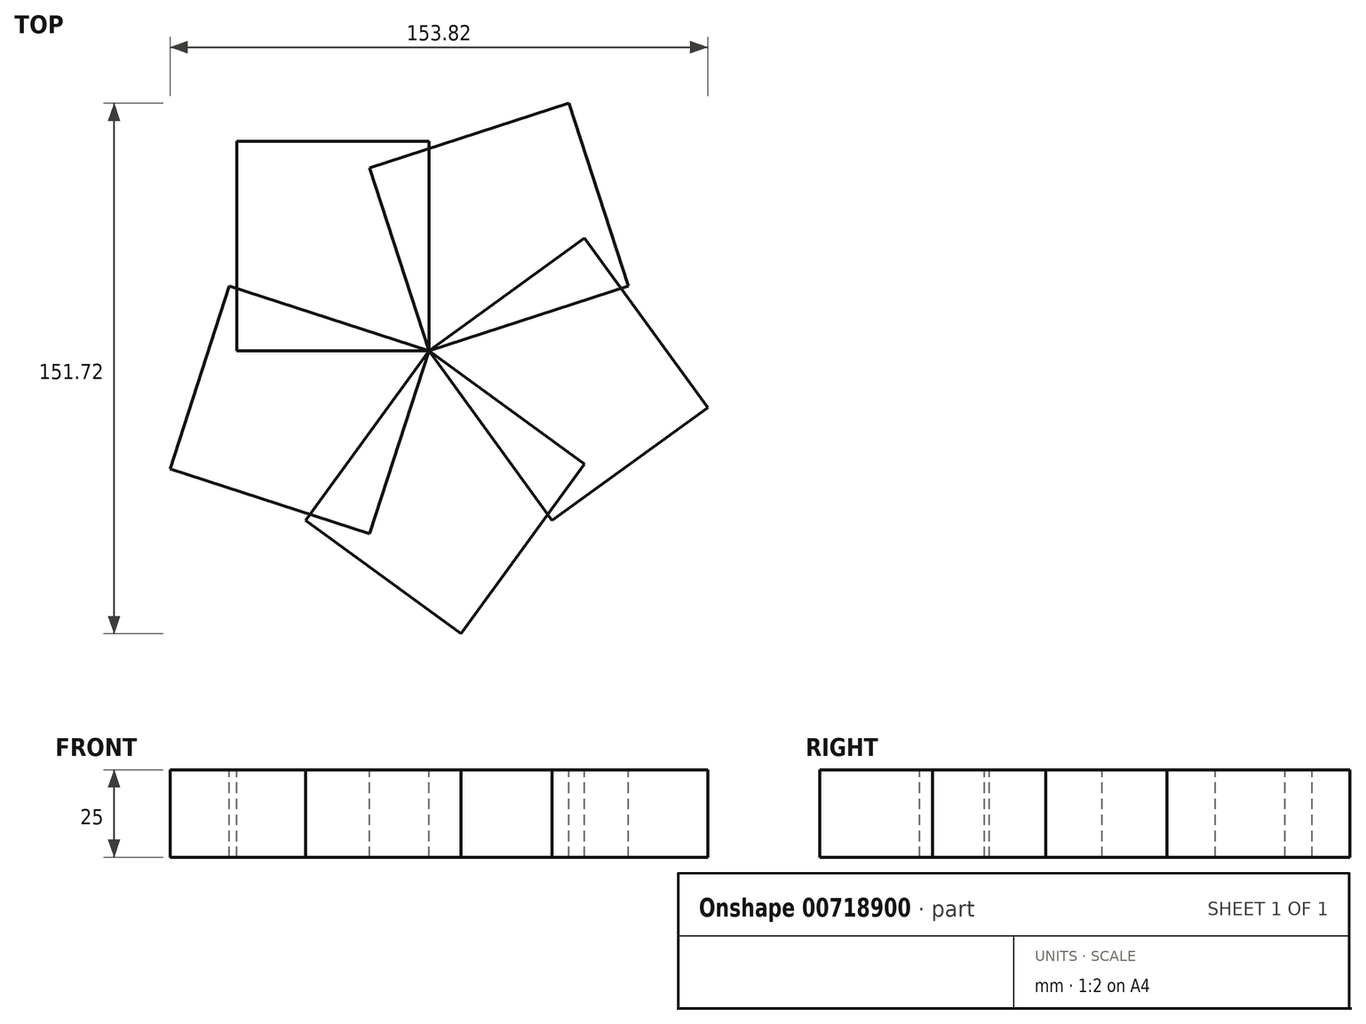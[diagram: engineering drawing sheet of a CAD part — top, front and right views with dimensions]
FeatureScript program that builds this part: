
annotation { "Feature Type Name" : "Feature", "Feature Type Description" : "" }
export const myFeature = defineFeature(function(context is Context, id is Id, definition is map)
    precondition{}
    {
        {
            var Q0;
            Q0=qCreatedBy(makeId("Top.planeOp"),FACE);
            var sketch = newSketch(context, id + "F0", { "sketchPlane" : qUnion([Q0])});
            skLineSegment(sketch, "E0.bottom", {"start": v(-55, 60) * mm, "end": v(0, 60) * mm});
            skLineSegment(sketch, "E0.top", {"start": v(-55, 0) * mm, "end": v(0, 0) * mm});
            skLineSegment(sketch, "E0.left", {"start": v(-55, 60) * mm, "end": v(-55, 0) * mm});
            skLineSegment(sketch, "E0.right", {"start": v(0, 60) * mm, "end": v(0, 0) * mm});
            skSolve(sketch);
        }
        {
            var Q0;
            Q0 = qSketchRegion(id + "F0", true);
            extrude(context, id + "F1", {"entities" : qUnion([Q0]), "oppositeDirection" : true, "depth" : 25 * mm, "offsetDistance" : 25 * mm});
        }
        {
            var Q0;
            Q0=makeQuery(id+"F1.opExtrude","SWEPT_BODY",BODY,{"disambiguationData":[OSD([sQuery(id+"F0.wireOp",EDGE,"E0.bottom"),sQuery(id+"F0.wireOp",EDGE,"E0.top"),sQuery(id+"F0.wireOp",EDGE,"E0.left"),sQuery(id+"F0.wireOp",EDGE,"E0.right")])]});
            var Q1;
            Q1=makeQuery(id+"F1.opExtrude","SWEPT_EDGE",EDGE,{"disambiguationData":[OSD([sQuery(id+"F0.wireOp",EDGE,"E0.top"),sQuery(id+"F0.wireOp",EDGE,"E0.right")])]});
            circularPattern(context, id + "F2", {"entities" : qUnion([Q0]), "axis" : qUnion([Q1]), "angle" : 360 * degree, "instanceCount" : 5, "equalSpace" : true});
        }
    });
